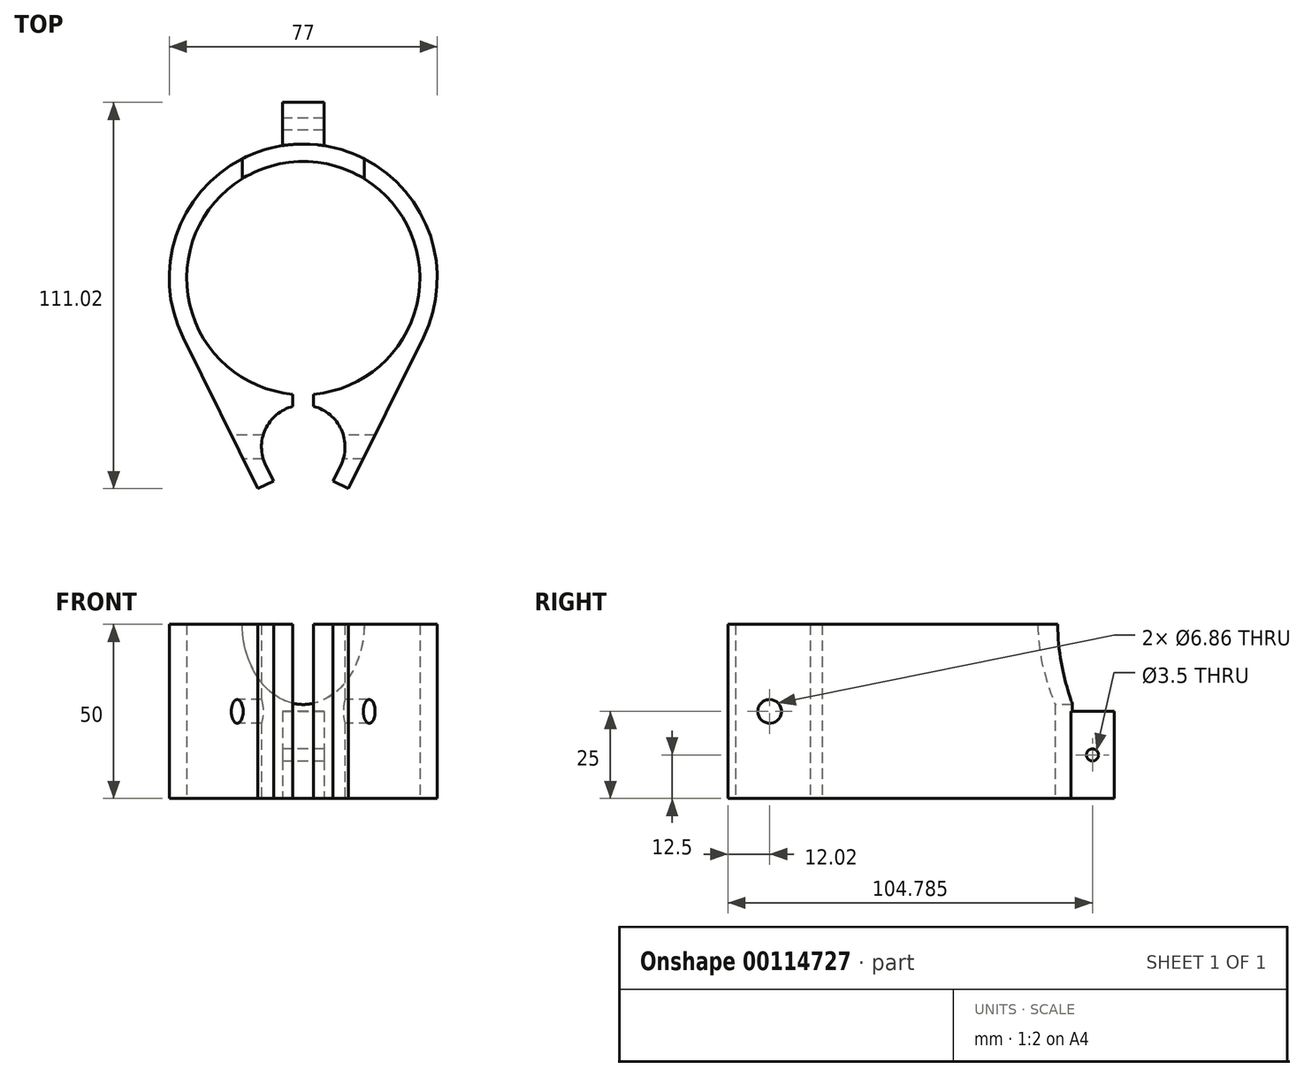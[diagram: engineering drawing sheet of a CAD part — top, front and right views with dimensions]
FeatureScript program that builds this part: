
annotation { "Feature Type Name" : "Feature", "Feature Type Description" : "" }
export const myFeature = defineFeature(function(context is Context, id is Id, definition is map)
    precondition{}
    {
        {
            var Q0;
            Q0=qCreatedBy(makeId("Top.planeOp"),FACE);
            var sketch = newSketch(context, id + "F0", { "sketchPlane" : qUnion([Q0])});
            skCircle(sketch, "E0", {"center": v(0, 0) * mm, "radius": 12 * mm});
            skCircle(sketch, "E1", {"center": v(0, 48.5) * mm, "radius": 33.5 * mm});
            skLineSegment(sketch, "E2.0", {"start": v(-34.51, 31.43) * mm, "end": v(-15.24, -7.54) * mm});
            skLineSegment(sketch, "E3.0", {"start": v(15.24, -7.54) * mm, "end": v(34.51, 31.43) * mm});
            skArc(sketch, "E4.0", {"start": v(-15.24, -7.54) * mm, "mid": v(0, -17) * mm, "end": v(15.24, -7.54) * mm});
            skArc(sketch, "E5.trimOffspring", {"start": v(34.51, 31.43) * mm, "mid": v(0, 87) * mm, "end": v(-34.51, 31.43) * mm});
            skSolve(sketch);
        }
        {
            var Q0;
            Q0=qSketchRegion(id+"F0",true);
            extrude(context, id + "F1", {"entities" : qUnion([Q0]), "depth" : 50 * mm});
        }
        {
            var Q0;
            Q0=qCreatedBy(makeId("Front.planeOp"),FACE);
            cPlane(context, id + "F2", {"entities" : qUnion([Q0]), "cplaneType" : CPlaneType.OFFSET, "offset" : 87 * mm, "oppositeDirection" : true, "width" : 150 * mm, "height" : 150 * mm});
        }
        {
            var Q0;
            Q0=qCreatedBy(id+"F2.planeOp",FACE);
            var sketch = newSketch(context, id + "F3", { "sketchPlane" : qUnion([Q0])});
            skLineSegment(sketch, "E6.0", {"start": v(-38.5, 50) * mm, "end": v(38.5, 50) * mm});
            skEllipse(sketch, "E7", {"center": v(0, 50) * mm, "majorRadius": 23 * mm, "minorRadius": 17.5 * mm, "majorAxis": v(0, -1)});
            skSolve(sketch);
        }
        {
            var Q0;
            Q0=qSketchRegion(id+"F3",true);
            extrude(context, id + "F4", {"entities" : qUnion([Q0]), "operationType" : NewBodyOperationType.REMOVE, "depth" : 25 * mm});
        }
        {
            var Q0;
            Q0=qCreatedBy(id+"F2.planeOp",FACE);
            var sketch = newSketch(context, id + "F5", { "sketchPlane" : qUnion([Q0])});
            skLineSegment(sketch, "E8.bottom", {"start": v(6, 0) * mm, "end": v(-6, 0) * mm});
            skLineSegment(sketch, "E8.top", {"start": v(6, 25) * mm, "end": v(-6, 25) * mm});
            skLineSegment(sketch, "E8.left", {"start": v(6, 0) * mm, "end": v(6, 25) * mm});
            skLineSegment(sketch, "E8.right", {"start": v(-6, 0) * mm, "end": v(-6, 25) * mm});
            skSolve(sketch);
        }
        {
            var Q0;
            Q0=qSketchRegion(id+"F5",true);
            extrude(context, id + "F6", {"entities" : qUnion([Q0]), "operationType" : NewBodyOperationType.ADD, "depth" : 1 * mm});
        }
        {
            var Q0;
            Q0=qSketchRegion(id+"F5",true);
            extrude(context, id + "F7", {"entities" : qUnion([Q0]), "operationType" : NewBodyOperationType.ADD, "oppositeDirection" : true, "depth" : 12 * mm});
        }
        {
            var Q0;
            Q0=qCreatedBy(makeId("Right.planeOp"),FACE);
            var sketch = newSketch(context, id + "F8", { "sketchPlane" : qUnion([Q0])});
            skLineSegment(sketch, "E9.0", {"start": v(31.43, 50) * mm, "end": v(-7.54, 50) * mm});
            skLineSegment(sketch, "E10.0", {"start": v(31.43, 0) * mm, "end": v(-7.54, 0) * mm});
            skPoint(sketch, "E11", {"position": v(0, 50) * mm});
            skLineSegment(sketch, "E12", {"start": v(0, 50) * mm, "end": v(0, 0) * mm, "construction": true});
            skCircle(sketch, "E13", {"center": v(0, 25) * mm, "radius": 3.43 * mm});
            skSolve(sketch);
        }
        {
            var Q0;
            Q0=qSketchRegion(id+"F8",true);
            extrude(context, id + "F9", {"entities" : qUnion([Q0]), "operationType" : NewBodyOperationType.REMOVE, "endBound" : BoundingType.SYMMETRIC, "depth" : 60 * mm});
        }
        {
            var Q0;
            {var subQ0=sQuery(id+"F5.wireOp",EDGE,"E8.right");Q0=makeQuery(id+"F7.boolean.opBoolean","MERGE",FACE,{"derivedFrom":[makeQuery(id+"F6.opExtrude","SWEPT_FACE",FACE,{"disambiguationData":[OSD([subQ0])]}),makeQuery(id+"F7.opExtrude","SWEPT_FACE",FACE,{"disambiguationData":[OSD([subQ0])]})]});}
            var sketch = newSketch(context, id + "F10", { "sketchPlane" : qUnion([Q0])});
            skLineSegment(sketch, "E14", {"start": v(-92.76, 25) * mm, "end": v(-92.76, 0) * mm, "construction": true});
            skLineSegment(sketch, "E15", {"start": v(-99, 12.5) * mm, "end": v(-92.76, 12.5) * mm, "construction": true});
            skCircle(sketch, "E16", {"center": v(-92.76, 12.5) * mm, "radius": 1.75 * mm});
            skPoint(sketch, "E17.0.start.orphan", {"position": v(-86.53, 25) * mm});
            skPoint(sketch, "E18.orphan", {"position": v(-99, 25) * mm});
            skPoint(sketch, "E19.orphan", {"position": v(-99, 0) * mm});
            skPoint(sketch, "E20.0.start.orphan", {"position": v(-86.53, 0) * mm});
            skSolve(sketch);
        }
        {
            var Q0;
            Q0=qSketchRegion(id+"F10",true);
            extrude(context, id + "F11", {"entities" : qUnion([Q0]), "operationType" : NewBodyOperationType.REMOVE, "oppositeDirection" : true, "depth" : 25 * mm});
        }
        {
            var Q0;
            Q0=makeQuery(id+"F1.opExtrude","CAP_FACE",FACE,{"disambiguationData":[OSD([sQuery(id+"F0.wireOp",EDGE,"E0"),sQuery(id+"F0.wireOp",EDGE,"E1"),sQuery(id+"F0.wireOp",EDGE,"E2.0"),sQuery(id+"F0.wireOp",EDGE,"E3.0"),sQuery(id+"F0.wireOp",EDGE,"E4.0"),sQuery(id+"F0.wireOp",EDGE,"E5.trimOffspring")])],"isStart":false});
            var sketch = newSketch(context, id + "F12", { "sketchPlane" : qUnion([Q0])});
            skLineSegment(sketch, "E21.bottom", {"start": v(-3, 17.8) * mm, "end": v(3, 17.8) * mm});
            skLineSegment(sketch, "E21.top", {"start": v(-3, 9.03) * mm, "end": v(3, 9.03) * mm});
            skLineSegment(sketch, "E21.left", {"start": v(-3, 17.8) * mm, "end": v(-3, 9.03) * mm});
            skLineSegment(sketch, "E21.right", {"start": v(3, 17.8) * mm, "end": v(3, 9.03) * mm});
            skSolve(sketch);
        }
        {
            var Q0;
            Q0=qSketchRegion(id+"F12",true);
            extrude(context, id + "F13", {"entities" : qUnion([Q0]), "operationType" : NewBodyOperationType.REMOVE, "oppositeDirection" : true, "depth" : 55 * mm});
        }
        {
            var Q0;
            Q0=makeQuery(id+"F1.opExtrude","CAP_FACE",FACE,{"disambiguationData":[OSD([sQuery(id+"F0.wireOp",EDGE,"E0"),sQuery(id+"F0.wireOp",EDGE,"E1"),sQuery(id+"F0.wireOp",EDGE,"E2.0"),sQuery(id+"F0.wireOp",EDGE,"E3.0"),sQuery(id+"F0.wireOp",EDGE,"E4.0"),sQuery(id+"F0.wireOp",EDGE,"E5.trimOffspring")])],"isStart":false});
            var sketch = newSketch(context, id + "F14", { "sketchPlane" : qUnion([Q0])});
            skArc(sketch, "E22.0", {"start": v(-10.76, -5.32) * mm, "mid": v(0, -12) * mm, "end": v(10.76, -5.32) * mm});
            skArc(sketch, "E23.0", {"start": v(-15.24, -7.54) * mm, "mid": v(0, -17) * mm, "end": v(15.24, -7.54) * mm});
            skLineSegment(sketch, "E24", {"start": v(-15.24, -7.54) * mm, "end": v(-10.76, -5.32) * mm});
            skLineSegment(sketch, "E25", {"start": v(15.24, -7.54) * mm, "end": v(10.76, -5.32) * mm});
            skPoint(sketch, "E26.orphan", {"position": v(3, 11.62) * mm});
            skPoint(sketch, "E27.orphan", {"position": v(-3, 11.62) * mm});
            skSolve(sketch);
        }
        {
            var Q0;
            Q0=qSketchRegion(id+"F14",true);
            extrude(context, id + "F15", {"entities" : qUnion([Q0]), "operationType" : NewBodyOperationType.REMOVE, "oppositeDirection" : true, "depth" : 52 * mm});
        }
        {
            var Q0;
            Q0=qCreatedBy(makeId("Top.planeOp"),FACE);
            var sketch = newSketch(context, id + "F16", { "sketchPlane" : qUnion([Q0])});
            skLineSegment(sketch, "E28.0", {"start": v(-15.24, -7.54) * mm, "end": v(-10.76, -5.32) * mm});
            skLineSegment(sketch, "E29", {"start": v(-15.24, -7.54) * mm, "end": v(-13.02, -12.02) * mm});
            skLineSegment(sketch, "E30", {"start": v(-10.76, -5.32) * mm, "end": v(-8.54, -9.8) * mm});
            skLineSegment(sketch, "E31", {"start": v(-13.02, -12.02) * mm, "end": v(-8.54, -9.8) * mm});
            skPoint(sketch, "E32.0.end.orphan", {"position": v(10.76, -5.32) * mm});
            skPoint(sketch, "E33.0.end.orphan", {"position": v(34.51, 31.43) * mm});
            skPoint(sketch, "E33.0.start.orphan", {"position": v(15.24, -7.54) * mm});
            skPoint(sketch, "E34.0.start.orphan", {"position": v(-34.51, 31.43) * mm});
            skLineSegment(sketch, "E35.MirrorCS", {"start": v(15.24, -7.54) * mm, "end": v(10.76, -5.32) * mm});
            skLineSegment(sketch, "E36.MirrorCS", {"start": v(10.76, -5.32) * mm, "end": v(8.54, -9.8) * mm});
            skLineSegment(sketch, "E37.MirrorCS", {"start": v(13.02, -12.02) * mm, "end": v(8.54, -9.8) * mm});
            skLineSegment(sketch, "E38.MirrorCS", {"start": v(15.24, -7.54) * mm, "end": v(13.02, -12.02) * mm});
            skSolve(sketch);
        }
        {
            var Q0;
            Q0=qSketchRegion(id+"F16",true);
            extrude(context, id + "F17", {"entities" : qUnion([Q0]), "operationType" : NewBodyOperationType.ADD, "depth" : 50 * mm});
        }
    });
